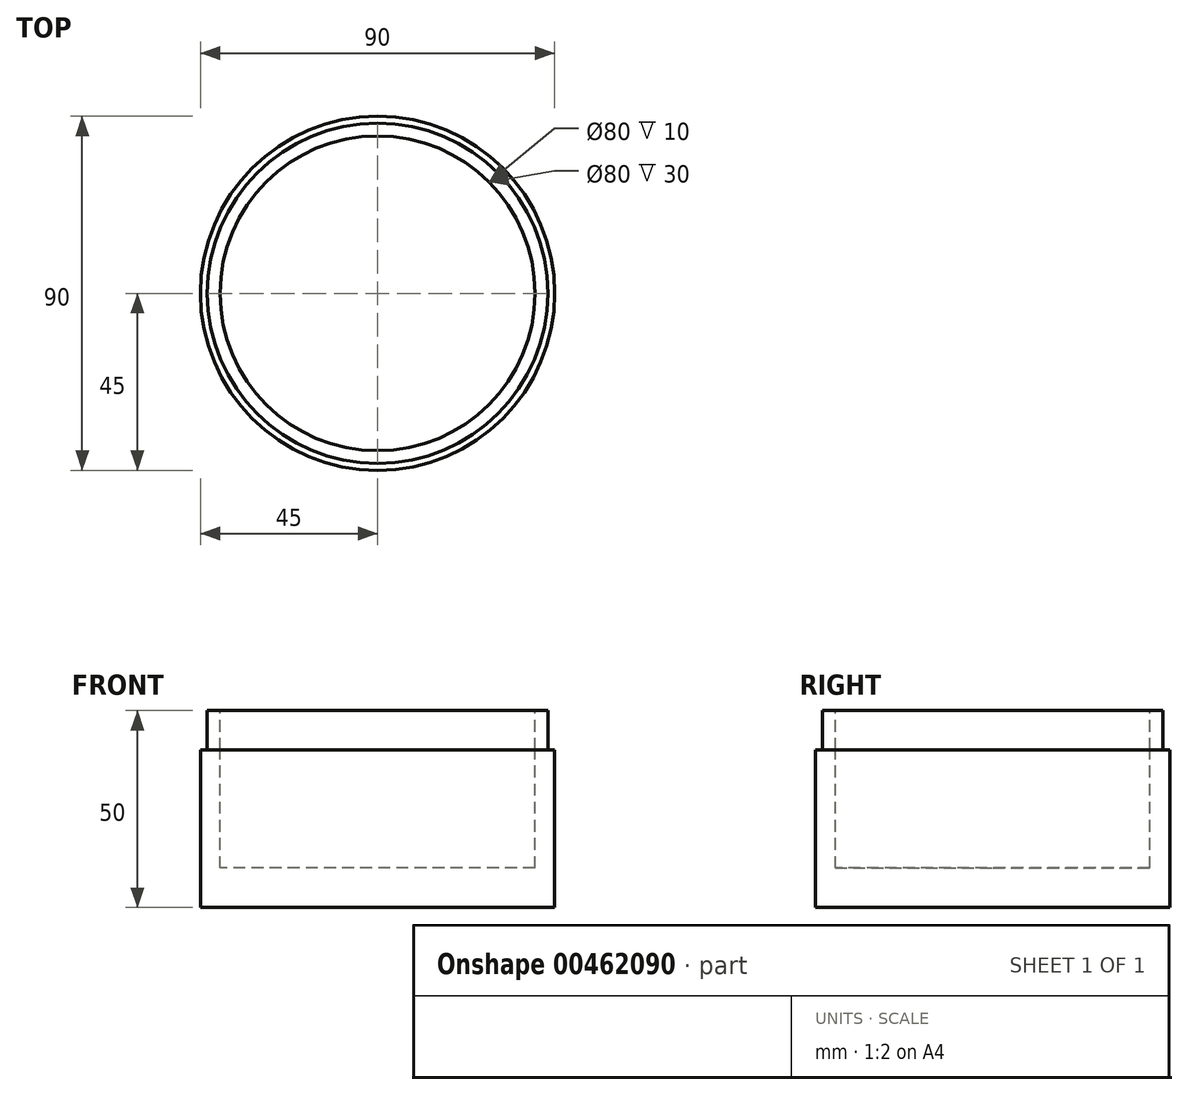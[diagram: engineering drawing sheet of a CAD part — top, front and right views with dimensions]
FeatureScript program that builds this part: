
annotation { "Feature Type Name" : "Feature", "Feature Type Description" : "" }
export const myFeature = defineFeature(function(context is Context, id is Id, definition is map)
    precondition{}
    {
        {
            var Q0;
            Q0=qCreatedBy(makeId("Top.planeOp"),FACE);
            var sketch = newSketch(context, id + "F0", { "sketchPlane" : qUnion([Q0])});
            skCircle(sketch, "E0", {"center": v(0, 0) * mm, "radius": 45 * mm});
            skSolve(sketch);
        }
        {
            var Q0;
            Q0 = qSketchRegion(id + "F0", true);
            extrude(context, id + "F1", {"entities" : qUnion([Q0]), "depth" : 40 * mm});
        }
        {
            var Q0;
            Q0=makeQuery(id+"F1.opExtrude","CAP_FACE",FACE,{"disambiguationData":[OSD([sQuery(id+"F0.wireOp",EDGE,"E0")])],"isStart":false});
            var sketch = newSketch(context, id + "F2", { "sketchPlane" : qUnion([Q0])});
            skCircle(sketch, "E1", {"center": v(0, 0) * mm, "radius": 43.25 * mm});
            skSolve(sketch);
        }
        {
            var Q0;
            Q0=makeQuery(id+"F2.imprint","IMPRINT",FACE,{"disambiguationData":[TD([[makeQuery(id+"F2.imprint","IMPRINT",EDGE,{"derivedFrom":sQuery(id+"F2.wireOp",EDGE,"E1")}),1.0]])]});
            extrude(context, id + "F3", {"entities" : qUnion([Q0]), "depth" : 10 * mm});
        }
        {
            var Q0;
            Q0=makeQuery(id+"F3.opExtrude","CAP_FACE",FACE,{"disambiguationData":[OSD([sQuery(id+"F2.wireOp",EDGE,"E1")])],"isStart":false});
            var sketch = newSketch(context, id + "F4", { "sketchPlane" : qUnion([Q0])});
            skCircle(sketch, "E2", {"center": v(0, 0) * mm, "radius": 40 * mm});
            skSolve(sketch);
        }
        {
            var Q0;
            Q0=makeQuery(id+"F4.imprint","IMPRINT",FACE,{"disambiguationData":[TD([[makeQuery(id+"F4.imprint","IMPRINT",EDGE,{"derivedFrom":sQuery(id+"F4.wireOp",EDGE,"E2")}),1.0]])]});
            extrude(context, id + "F5", {"entities" : qUnion([Q0]), "operationType" : NewBodyOperationType.REMOVE, "oppositeDirection" : true, "depth" : 40 * mm});
        }
    });
